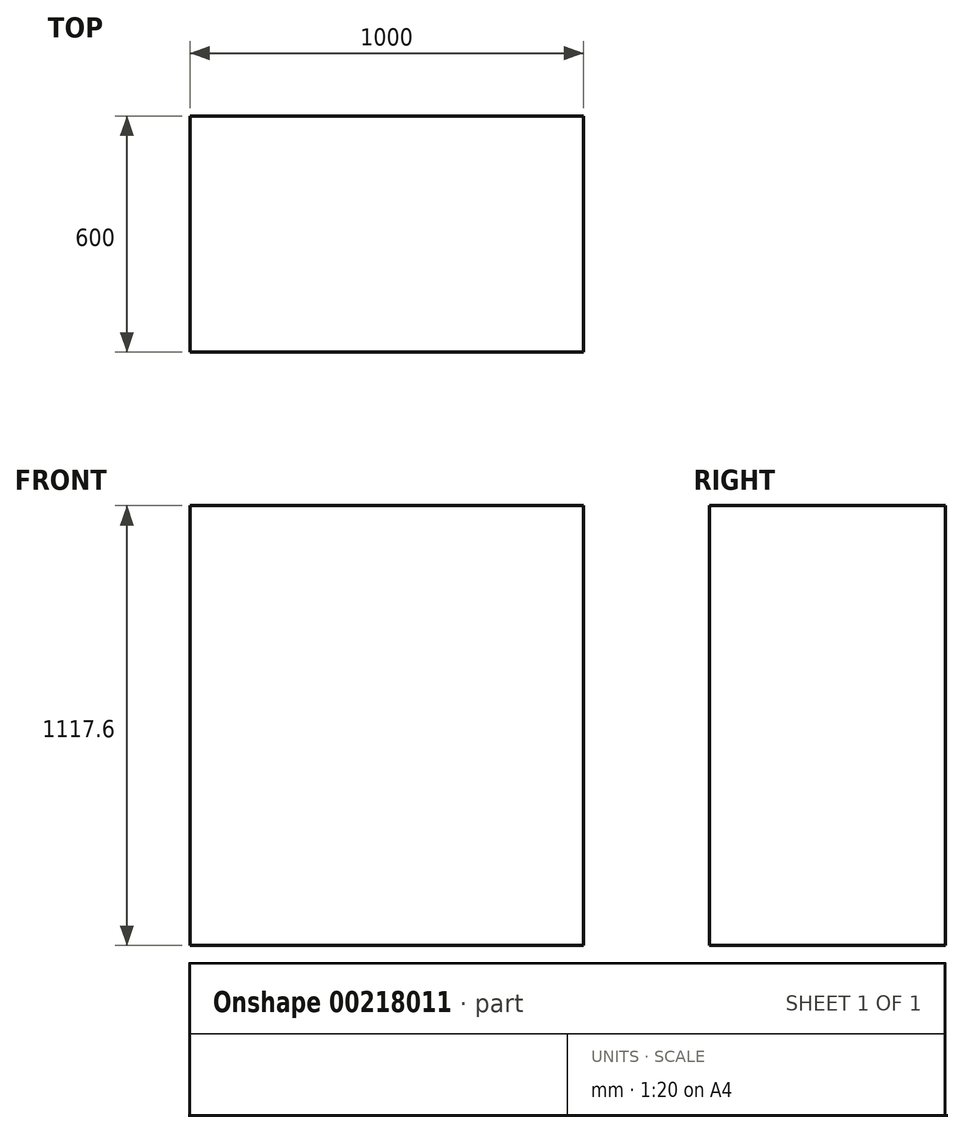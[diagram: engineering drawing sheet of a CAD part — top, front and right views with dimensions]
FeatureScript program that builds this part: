
annotation { "Feature Type Name" : "Feature", "Feature Type Description" : "" }
export const myFeature = defineFeature(function(context is Context, id is Id, definition is map)
    precondition{}
    {
        {
            var Q0;
            Q0=qCreatedBy(makeId("Top.planeOp"),FACE);
            var sketch = newSketch(context, id + "F0", { "sketchPlane" : qUnion([Q0])});
            skLineSegment(sketch, "E0.bottom", {"start": v(0, 0) * mm, "end": v(1000, 0) * mm});
            skLineSegment(sketch, "E0.top", {"start": v(0, 600) * mm, "end": v(1000, 600) * mm});
            skLineSegment(sketch, "E0.left", {"start": v(0, 0) * mm, "end": v(0, 600) * mm});
            skLineSegment(sketch, "E0.right", {"start": v(1000, 0) * mm, "end": v(1000, 600) * mm});
            skSolve(sketch);
        }
        {
            var Q0;
            Q0 = qSketchRegion(id + "F0", true);
            extrude(context, id + "F1", {"entities" : qUnion([Q0]), "depth" : 1117.6 * mm, "offsetDistance" : 25.4 * mm});
        }
    });
